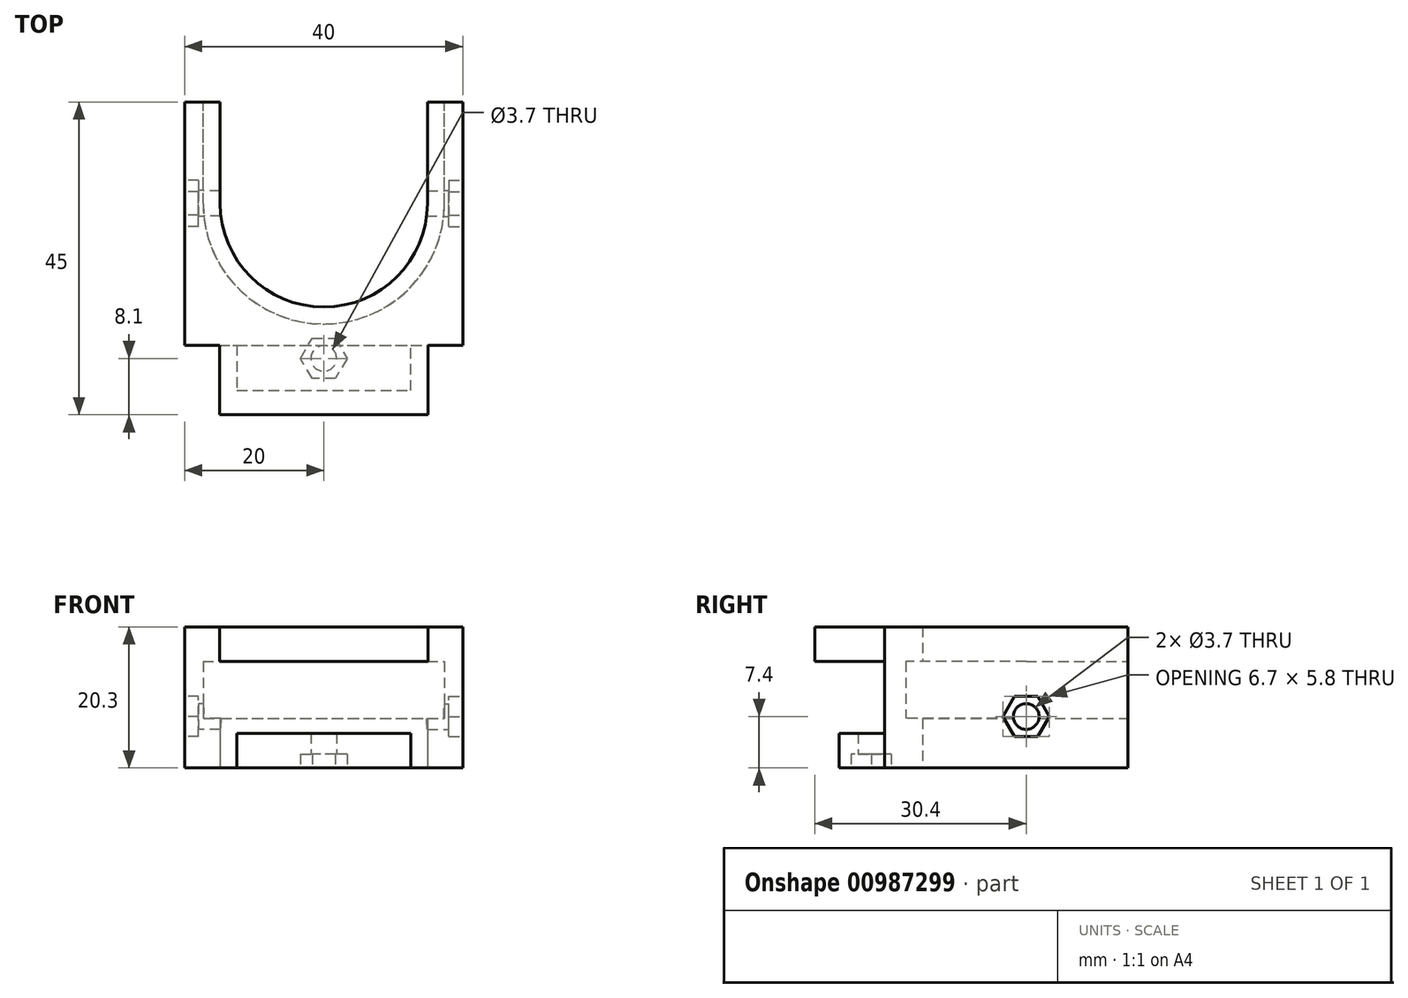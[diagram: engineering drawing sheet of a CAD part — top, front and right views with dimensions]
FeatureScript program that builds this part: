
annotation { "Feature Type Name" : "Feature", "Feature Type Description" : "" }
export const myFeature = defineFeature(function(context is Context, id is Id, definition is map)
    precondition{}
    {
        {
            var Q0;
            Q0=qCreatedBy(makeId("Top.planeOp"),FACE);
            var sketch = newSketch(context, id + "F0", { "sketchPlane" : qUnion([Q0])});
            skLineSegment(sketch, "E0.bottom", {"start": v(-20, 24) * mm, "end": v(-14.9, 24) * mm});
            skLineSegment(sketch, "E0.top", {"start": v(-12.5, -11) * mm, "end": v(20, -11) * mm});
            skLineSegment(sketch, "E0.left", {"start": v(-20, 24) * mm, "end": v(-20, -11) * mm});
            skLineSegment(sketch, "E0.right", {"start": v(20, 24) * mm, "end": v(20, -11) * mm});
            skLineSegment(sketch, "E1.right", {"start": v(-12.5, -11) * mm, "end": v(-12.5, -17.5) * mm});
            skLineSegment(sketch, "E2.bottom", {"start": v(-12.5, -17.5) * mm, "end": v(12.5, -17.5) * mm});
            skLineSegment(sketch, "E2.top", {"start": v(-12.5, -17.5) * mm, "end": v(12.5, -17.5) * mm});
            skLineSegment(sketch, "E2.left", {"start": v(-12.5, -17.5) * mm, "end": v(-12.5, -17.5) * mm});
            skLineSegment(sketch, "E2.right", {"start": v(12.5, -17.5) * mm, "end": v(12.5, -17.5) * mm});
            skLineSegment(sketch, "E3.top", {"start": v(12.5, -11) * mm, "end": v(12.5, -11) * mm});
            skLineSegment(sketch, "E3.left", {"start": v(12.5, -17.5) * mm, "end": v(12.5, -11) * mm});
            skLineSegment(sketch, "E3.right", {"start": v(12.5, -17.5) * mm, "end": v(12.5, -11) * mm});
            skLineSegment(sketch, "E4", {"start": v(-20, -11) * mm, "end": v(-12.5, -11) * mm});
            skLineSegment(sketch, "E5", {"start": v(-20, 9.4) * mm, "end": v(20, 9.4) * mm, "construction": true});
            skArc(sketch, "E6", {"start": v(-14.9, 9.4) * mm, "mid": v(0, -5.5) * mm, "end": v(14.9, 9.4) * mm});
            skLineSegment(sketch, "E7", {"start": v(-14.9, 9.4) * mm, "end": v(-14.9, 24) * mm});
            skLineSegment(sketch, "E8", {"start": v(14.9, 9.4) * mm, "end": v(14.9, 24) * mm});
            skLineSegment(sketch, "E9.trimOffspring", {"start": v(14.9, 24) * mm, "end": v(20, 24) * mm});
            skCircle(sketch, "E10", {"center": v(0, -12.9) * mm, "radius": 1.85 * mm});
            skSolve(sketch);
        }
        {
            var Q0;
            Q0=qSketchRegion(id+"F0",true);
            extrude(context, id + "F1", {"entities" : qUnion([Q0]), "depth" : 5 * mm, "offsetDistance" : 25 * mm});
        }
        {
            var Q0;
            Q0=makeQuery(id+"F1.opExtrude","CAP_FACE",FACE,{"disambiguationData":[OSD([sQuery(id+"F0.wireOp",EDGE,"E0.bottom"),sQuery(id+"F0.wireOp",EDGE,"E0.top"),sQuery(id+"F0.wireOp",EDGE,"E0.left"),sQuery(id+"F0.wireOp",EDGE,"E0.right"),sQuery(id+"F0.wireOp",EDGE,"E1.right"),sQuery(id+"F0.wireOp",EDGE,"E2.top"),sQuery(id+"F0.wireOp",EDGE,"E3.right"),sQuery(id+"F0.wireOp",EDGE,"E4"),sQuery(id+"F0.wireOp",EDGE,"E6"),sQuery(id+"F0.wireOp",EDGE,"E7"),sQuery(id+"F0.wireOp",EDGE,"E8"),sQuery(id+"F0.wireOp",EDGE,"E9.trimOffspring")])],"isStart":false});
            var sketch = newSketch(context, id + "F2", { "sketchPlane" : qUnion([Q0])});
            skLineSegment(sketch, "E11.bottom", {"start": v(-20, 24) * mm, "end": v(-14.9, 24) * mm});
            skLineSegment(sketch, "E11.top", {"start": v(-20, -11) * mm, "end": v(20, -11) * mm});
            skLineSegment(sketch, "E11.left", {"start": v(-20, 24) * mm, "end": v(-20, -11) * mm});
            skLineSegment(sketch, "E11.right", {"start": v(20, 24) * mm, "end": v(20, -11) * mm});
            skLineSegment(sketch, "E12.bottom", {"start": v(14.9, 24) * mm, "end": v(14.9, 24) * mm});
            skLineSegment(sketch, "E12.top", {"start": v(14.9, 9.4) * mm, "end": v(14.9, 9.4) * mm});
            skLineSegment(sketch, "E12.left", {"start": v(14.9, 24) * mm, "end": v(14.9, 9.4) * mm});
            skLineSegment(sketch, "E12.right", {"start": v(14.9, 24) * mm, "end": v(14.9, 9.4) * mm});
            skLineSegment(sketch, "E13.bottom", {"start": v(-14.9, 24) * mm, "end": v(-14.9, 24) * mm});
            skLineSegment(sketch, "E13.top", {"start": v(-14.9, 9.4) * mm, "end": v(-14.9, 9.4) * mm});
            skLineSegment(sketch, "E13.left", {"start": v(-14.9, 24) * mm, "end": v(-14.9, 9.4) * mm});
            skLineSegment(sketch, "E13.right", {"start": v(-14.9, 24) * mm, "end": v(-14.9, 9.4) * mm});
            skLineSegment(sketch, "E14.trimOffspring", {"start": v(14.9, 24) * mm, "end": v(20, 24) * mm});
            skArc(sketch, "E15", {"start": v(-14.9, 9.4) * mm, "mid": v(0, -5.5) * mm, "end": v(14.9, 9.4) * mm});
            skSolve(sketch);
        }
        {
            var Q0;
            Q0=qSketchRegion(id+"F2",true);
            extrude(context, id + "F3", {"entities" : qUnion([Q0]), "operationType" : NewBodyOperationType.ADD, "depth" : 2.1 * mm, "offsetDistance" : 25 * mm});
        }
        {
            var Q0;
            Q0=makeQuery(id+"F3.opExtrude","CAP_FACE",FACE,{"disambiguationData":[OSD([sQuery(id+"F2.wireOp",EDGE,"E11.bottom"),sQuery(id+"F2.wireOp",EDGE,"E11.top"),sQuery(id+"F2.wireOp",EDGE,"E11.left"),sQuery(id+"F2.wireOp",EDGE,"E11.right"),sQuery(id+"F2.wireOp",EDGE,"E12.right"),sQuery(id+"F2.wireOp",EDGE,"E13.right"),sQuery(id+"F2.wireOp",EDGE,"E14.trimOffspring"),sQuery(id+"F2.wireOp",EDGE,"E15")])],"isStart":false});
            var sketch = newSketch(context, id + "F4", { "sketchPlane" : qUnion([Q0])});
            skLineSegment(sketch, "E16.bottom", {"start": v(-20, 24) * mm, "end": v(-17.35, 24) * mm});
            skLineSegment(sketch, "E16.top", {"start": v(-20, -11) * mm, "end": v(20, -11) * mm});
            skLineSegment(sketch, "E16.left", {"start": v(-20, 24) * mm, "end": v(-20, -11) * mm});
            skLineSegment(sketch, "E16.right", {"start": v(20, 24) * mm, "end": v(20, -11) * mm});
            skArc(sketch, "E17", {"start": v(-17.35, 9.4) * mm, "mid": v(0, -7.95) * mm, "end": v(17.35, 9.4) * mm});
            skLineSegment(sketch, "E18", {"start": v(-17.35, 9.4) * mm, "end": v(-17.35, 24) * mm});
            skLineSegment(sketch, "E19", {"start": v(17.35, 9.4) * mm, "end": v(17.35, 24) * mm});
            skLineSegment(sketch, "E20.trimOffspring", {"start": v(17.35, 24) * mm, "end": v(20, 24) * mm});
            skSolve(sketch);
        }
        {
            var Q0;
            Q0=qSketchRegion(id+"F4",true);
            extrude(context, id + "F5", {"entities" : qUnion([Q0]), "operationType" : NewBodyOperationType.ADD, "depth" : 8.2 * mm, "offsetDistance" : 25 * mm});
        }
        {
            var Q0;
            Q0=makeQuery(id+"F5.opExtrude","CAP_FACE",FACE,{"disambiguationData":[OSD([sQuery(id+"F4.wireOp",EDGE,"E16.bottom"),sQuery(id+"F4.wireOp",EDGE,"E16.top"),sQuery(id+"F4.wireOp",EDGE,"E16.left"),sQuery(id+"F4.wireOp",EDGE,"E16.right"),sQuery(id+"F4.wireOp",EDGE,"E17"),sQuery(id+"F4.wireOp",EDGE,"E18"),sQuery(id+"F4.wireOp",EDGE,"E19"),sQuery(id+"F4.wireOp",EDGE,"E20.trimOffspring")])],"isStart":false});
            var sketch = newSketch(context, id + "F6", { "sketchPlane" : qUnion([Q0])});
            skLineSegment(sketch, "E21.bottom", {"start": v(-20, 24) * mm, "end": v(-14.9, 24) * mm});
            skLineSegment(sketch, "E21.top", {"start": v(-20, -11) * mm, "end": v(-15, -11) * mm});
            skLineSegment(sketch, "E21.left", {"start": v(-20, 24) * mm, "end": v(-20, -11) * mm});
            skLineSegment(sketch, "E21.right", {"start": v(20, 24) * mm, "end": v(20, -11) * mm});
            skLineSegment(sketch, "E22.bottom", {"start": v(15, -21) * mm, "end": v(-15, -21) * mm});
            skLineSegment(sketch, "E22.left", {"start": v(15, -21) * mm, "end": v(15, -11) * mm});
            skLineSegment(sketch, "E22.right", {"start": v(-15, -21) * mm, "end": v(-15, -11) * mm});
            skLineSegment(sketch, "E23.trimOffspring", {"start": v(15, -11) * mm, "end": v(20, -11) * mm});
            skArc(sketch, "E24", {"start": v(-14.9, 9.4) * mm, "mid": v(0, -5.5) * mm, "end": v(14.9, 9.4) * mm});
            skLineSegment(sketch, "E25", {"start": v(-14.9, 9.4) * mm, "end": v(-14.9, 24) * mm});
            skLineSegment(sketch, "E26", {"start": v(14.9, 9.4) * mm, "end": v(14.9, 24) * mm});
            skLineSegment(sketch, "E27.trimOffspring", {"start": v(14.9, 24) * mm, "end": v(20, 24) * mm});
            skSolve(sketch);
        }
        {
            var Q0;
            Q0=qSketchRegion(id+"F6",true);
            var Q1;
            Q1=qSketchRegion(id+"F8",true);
            extrude(context, id + "F7", {"entities" : qUnion([Q0, Q1]), "operationType" : NewBodyOperationType.ADD, "depth" : 5 * mm, "offsetDistance" : 25 * mm});
        }
        {
            var Q0;
            Q0=makeQuery(id+"F7.boolean.opBoolean","MERGE",FACE,{"derivedFrom":[makeQuery(id+"F5.boolean.opBoolean","MERGE",FACE,{"derivedFrom":[makeQuery(id+"F3.boolean.opBoolean","MERGE",FACE,{"derivedFrom":[makeQuery(id+"F1.opExtrude","SWEPT_FACE",FACE,{"disambiguationData":[OSD([sQuery(id+"F0.wireOp",EDGE,"E0.left")])]}),makeQuery(id+"F3.opExtrude","SWEPT_FACE",FACE,{"disambiguationData":[OSD([sQuery(id+"F2.wireOp",EDGE,"E11.left")])]})]}),makeQuery(id+"F5.opExtrude","SWEPT_FACE",FACE,{"disambiguationData":[OSD([sQuery(id+"F4.wireOp",EDGE,"E16.left")])]})]}),makeQuery(id+"F7.opExtrude","SWEPT_FACE",FACE,{"disambiguationData":[OSD([sQuery(id+"F6.wireOp",EDGE,"E21.left")])]})]});
            var sketch = newSketch(context, id + "F8", { "sketchPlane" : qUnion([Q0])});
            skLineSegment(sketch, "E28", {"start": v(-9.4, 0) * mm, "end": v(-9.4, 20.3) * mm, "construction": true});
            skCircle(sketch, "E29.cCircle", {"center": v(-9.4, 7.4) * mm, "radius": 2.9 * mm});
            skLineSegment(sketch, "E29.0", {"start": v(-11.07, 4.5) * mm, "end": v(-12.75, 7.4) * mm});
            skLineSegment(sketch, "E29.1", {"start": v(-12.75, 7.4) * mm, "end": v(-11.07, 10.3) * mm});
            skLineSegment(sketch, "E29.2", {"start": v(-11.07, 10.3) * mm, "end": v(-7.73, 10.3) * mm});
            skLineSegment(sketch, "E29.3", {"start": v(-7.73, 10.3) * mm, "end": v(-6.05, 7.4) * mm});
            skLineSegment(sketch, "E29.4", {"start": v(-6.05, 7.4) * mm, "end": v(-7.73, 4.5) * mm});
            skLineSegment(sketch, "E29.5", {"start": v(-7.73, 4.5) * mm, "end": v(-11.07, 4.5) * mm});
            skPoint(sketch, "E29.0.midPoint", {"position": v(-11.91, 5.95) * mm});
            skSolve(sketch);
        }
        {
            var Q0;
            Q0=qSketchRegion(id+"F8",true);
            extrude(context, id + "F9", {"entities" : qUnion([Q0]), "operationType" : NewBodyOperationType.REMOVE, "oppositeDirection" : true, "depth" : 2 * mm, "offsetDistance" : 25 * mm});
        }
        {
            var Q0;
            Q0=makeQuery(id+"F7.boolean.opBoolean","MERGE",FACE,{"derivedFrom":[makeQuery(id+"F5.boolean.opBoolean","MERGE",FACE,{"derivedFrom":[makeQuery(id+"F3.boolean.opBoolean","MERGE",FACE,{"derivedFrom":[makeQuery(id+"F1.opExtrude","SWEPT_FACE",FACE,{"disambiguationData":[OSD([sQuery(id+"F0.wireOp",EDGE,"E0.right")])]}),makeQuery(id+"F3.opExtrude","SWEPT_FACE",FACE,{"disambiguationData":[OSD([sQuery(id+"F2.wireOp",EDGE,"E11.right")])]})]}),makeQuery(id+"F5.opExtrude","SWEPT_FACE",FACE,{"disambiguationData":[OSD([sQuery(id+"F4.wireOp",EDGE,"E16.right")])]})]}),makeQuery(id+"F7.opExtrude","SWEPT_FACE",FACE,{"disambiguationData":[OSD([sQuery(id+"F6.wireOp",EDGE,"E21.right")])]})]});
            var sketch = newSketch(context, id + "F10", { "sketchPlane" : qUnion([Q0])});
            skCircle(sketch, "E30.cCircle", {"center": v(9.4, 7.4) * mm, "radius": 2.9 * mm, "construction": true});
            skLineSegment(sketch, "E30.0", {"start": v(7.73, 10.3) * mm, "end": v(11.07, 10.3) * mm});
            skLineSegment(sketch, "E30.1", {"start": v(11.07, 10.3) * mm, "end": v(12.75, 7.4) * mm});
            skLineSegment(sketch, "E30.2", {"start": v(12.75, 7.4) * mm, "end": v(11.07, 4.5) * mm});
            skLineSegment(sketch, "E30.3", {"start": v(11.07, 4.5) * mm, "end": v(7.73, 4.5) * mm});
            skLineSegment(sketch, "E30.4", {"start": v(7.73, 4.5) * mm, "end": v(6.05, 7.4) * mm});
            skLineSegment(sketch, "E30.5", {"start": v(6.05, 7.4) * mm, "end": v(7.73, 10.3) * mm});
            skPoint(sketch, "E30.0.midPoint", {"position": v(9.4, 10.3) * mm});
            skSolve(sketch);
        }
        {
            var Q0;
            Q0=qSketchRegion(id+"F10",true);
            extrude(context, id + "F11", {"entities" : qUnion([Q0]), "operationType" : NewBodyOperationType.REMOVE, "oppositeDirection" : true, "depth" : 2 * mm, "offsetDistance" : 25 * mm});
        }
        {
            var Q0;
            Q0=makeQuery(id+"F11.boolean.opBoolean","COPY",FACE,{"derivedFrom":makeQuery(id+"F11.opExtrude","CAP_FACE",FACE,{"disambiguationData":[OSD([sQuery(id+"F10.wireOp",EDGE,"E30.0"),sQuery(id+"F10.wireOp",EDGE,"E30.1"),sQuery(id+"F10.wireOp",EDGE,"E30.2"),sQuery(id+"F10.wireOp",EDGE,"E30.3"),sQuery(id+"F10.wireOp",EDGE,"E30.4"),sQuery(id+"F10.wireOp",EDGE,"E30.5")])],"isStart":false})});
            var sketch = newSketch(context, id + "F12", { "sketchPlane" : qUnion([Q0])});
            skCircle(sketch, "E31", {"center": v(9.4, 7.4) * mm, "radius": 1.85 * mm});
            skSolve(sketch);
        }
        {
            var Q0;
            Q0=makeQuery(id+"F12.imprint","IMPRINT",FACE,{"disambiguationData":[TD([[makeQuery(id+"F12.imprint","IMPRINT",EDGE,{"derivedFrom":sQuery(id+"F12.wireOp",EDGE,"E31")}),1.0]])]});
            extrude(context, id + "F13", {"entities" : qUnion([Q0]), "operationType" : NewBodyOperationType.REMOVE, "oppositeDirection" : true, "depth" : 5 * mm, "offsetDistance" : 25 * mm});
        }
        {
            var Q0;
            Q0=makeQuery(id+"F9.boolean.opBoolean","COPY",FACE,{"derivedFrom":makeQuery(id+"F9.opExtrude","CAP_FACE",FACE,{"disambiguationData":[OSD([sQuery(id+"F8.wireOp",EDGE,"E29.0"),sQuery(id+"F8.wireOp",EDGE,"E29.1"),sQuery(id+"F8.wireOp",EDGE,"E29.2"),sQuery(id+"F8.wireOp",EDGE,"E29.3"),sQuery(id+"F8.wireOp",EDGE,"E29.4"),sQuery(id+"F8.wireOp",EDGE,"E29.5")])],"isStart":false})});
            var sketch = newSketch(context, id + "F14", { "sketchPlane" : qUnion([Q0])});
            skCircle(sketch, "E32", {"center": v(-9.4, 7.4) * mm, "radius": 1.85 * mm});
            skSolve(sketch);
        }
        {
            var Q0;
            Q0=makeQuery(id+"F14.imprint","IMPRINT",FACE,{"disambiguationData":[TD([[makeQuery(id+"F14.imprint","IMPRINT",EDGE,{"derivedFrom":sQuery(id+"F14.wireOp",EDGE,"E32")}),1.0]])]});
            var Q1;
            Q1=sQuery(id+"F14.wireOp",EDGE,"E32");
            extrude(context, id + "F15", {"entities" : qUnion([Q0]), "operationType" : NewBodyOperationType.REMOVE, "surfaceEntities" : qUnion([Q1]), "oppositeDirection" : true, "depth" : 5 * mm, "offsetDistance" : 25 * mm});
        }
        {
            var Q0;
            Q0=qCreatedBy(makeId("Top.planeOp"),FACE);
            var sketch = newSketch(context, id + "F16", { "sketchPlane" : qUnion([Q0])});
            skCircle(sketch, "E33.cCircle", {"center": v(0, -12.9) * mm, "radius": 2.9 * mm, "construction": true});
            skLineSegment(sketch, "E33.0", {"start": v(1.67, -15.8) * mm, "end": v(-1.67, -15.8) * mm});
            skLineSegment(sketch, "E33.1", {"start": v(-1.67, -15.8) * mm, "end": v(-3.35, -12.9) * mm});
            skLineSegment(sketch, "E33.2", {"start": v(-3.35, -12.9) * mm, "end": v(-1.67, -10) * mm});
            skLineSegment(sketch, "E33.3", {"start": v(-1.67, -10) * mm, "end": v(1.67, -10) * mm});
            skLineSegment(sketch, "E33.4", {"start": v(1.67, -10) * mm, "end": v(3.35, -12.9) * mm});
            skLineSegment(sketch, "E33.5", {"start": v(3.35, -12.9) * mm, "end": v(1.67, -15.8) * mm});
            skPoint(sketch, "E33.0.midPoint", {"position": v(0, -15.8) * mm});
            skSolve(sketch);
        }
        {
            var Q0;
            Q0=qSketchRegion(id+"F16",true);
            extrude(context, id + "F17", {"entities" : qUnion([Q0]), "operationType" : NewBodyOperationType.REMOVE, "depth" : 2 * mm, "offsetDistance" : 25 * mm});
        }
    });
